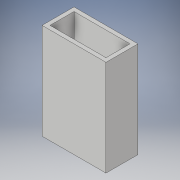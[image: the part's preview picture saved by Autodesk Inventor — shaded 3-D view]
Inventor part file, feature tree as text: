
AUTODESK INVENTOR PART (.ipt)
format: ipt  version: 2018 (Build 220112000, 112)  size: 96,768 bytes
history: native  units: in
note: dims shown in document units (in); Inventor stores cm internally (conversion verified against a paired STEP export)
features: extrude x1, sketch x1
ambient origin geometry x8: Origin, YZ Plane, XZ Plane, XY Plane, X Axis, Y Axis, Z Axis, Center Point
bodies: Solid1 (feature_tree)
feature tree (2):
  extrude  "Extrusion1"  Depth=2.0in
  sketch  "Sketch1"  dims[d0=1.0in d1=2.0in d2=0.125in d3=0.125in d4=0.125in d5=0.125in d6=3.0in d7=0.0in]
